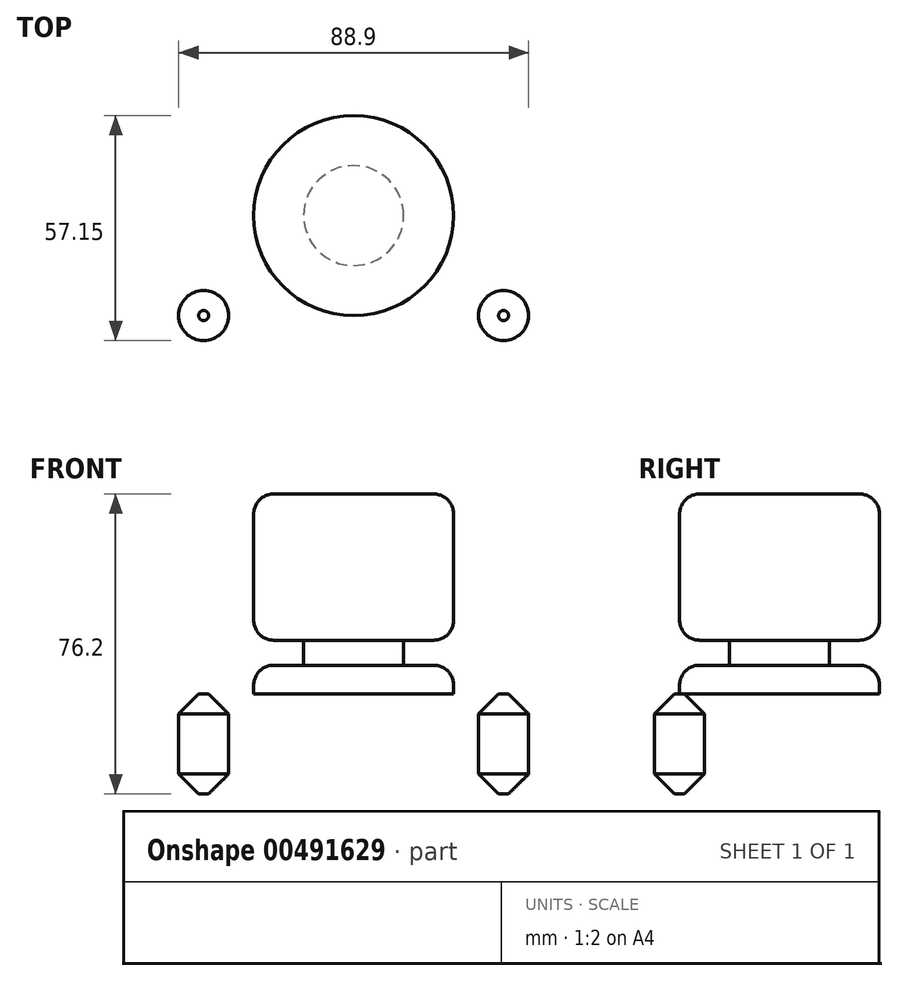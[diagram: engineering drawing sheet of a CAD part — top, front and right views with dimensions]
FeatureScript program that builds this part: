
annotation { "Feature Type Name" : "Feature", "Feature Type Description" : "" }
export const myFeature = defineFeature(function(context is Context, id is Id, definition is map)
    precondition{}
    {
        {
            var Q0;
            Q0=qCreatedBy(makeId("Top.planeOp"),FACE);
            var sketch = newSketch(context, id + "F0", { "sketchPlane" : qUnion([Q0])});
            skLineSegment(sketch, "E0.bottom", {"start": v(50.8, 38.1) * mm, "end": v(-50.8, 38.1) * mm});
            skLineSegment(sketch, "E0.top", {"start": v(50.8, -38.1) * mm, "end": v(-50.8, -38.1) * mm});
            skLineSegment(sketch, "E0.left", {"start": v(50.8, 38.1) * mm, "end": v(50.8, -38.1) * mm});
            skLineSegment(sketch, "E0.right", {"start": v(-50.8, 38.1) * mm, "end": v(-50.8, -38.1) * mm});
            skPoint(sketch, "E0.middle", {"position": v(0, 0) * mm});
            skSolve(sketch);
        }
        {
            var Q0;
            Q0 = qSketchRegion(id + "F0", true);
            extrude(context, id + "F1", {"entities" : qUnion([Q0]), "depth" : 25.4 * mm});
        }
        {
            var Q0;
            Q0=makeQuery(id+"F1.opExtrude","CAP_FACE",FACE,{"disambiguationData":[OSD([sQuery(id+"F0.wireOp",EDGE,"E0.bottom"),sQuery(id+"F0.wireOp",EDGE,"E0.top"),sQuery(id+"F0.wireOp",EDGE,"E0.left"),sQuery(id+"F0.wireOp",EDGE,"E0.right")])],"isStart":false});
            var sketch = newSketch(context, id + "F2", { "sketchPlane" : qUnion([Q0])});
            skCircle(sketch, "E1", {"center": v(-38.1, 25.4) * mm, "radius": 6.35 * mm});
            skCircle(sketch, "E2", {"center": v(38.1, 25.4) * mm, "radius": 6.35 * mm});
            skCircle(sketch, "E3.MirrorC", {"center": v(38.1, -25.4) * mm, "radius": 6.35 * mm});
            skCircle(sketch, "E4.MirrorC", {"center": v(-38.1, -25.4) * mm, "radius": 6.35 * mm});
            skSolve(sketch);
        }
        {
            var Q0;
            Q0=makeQuery(id+"F2.imprint","IMPRINT",FACE,{"disambiguationData":[TD([[makeQuery(id+"F2.imprint","IMPRINT",EDGE,{"derivedFrom":sQuery(id+"F2.wireOp",EDGE,"E1")}),1.0]])]});
            var Q1;
            Q1=makeQuery(id+"F2.imprint","IMPRINT",FACE,{"disambiguationData":[TD([[makeQuery(id+"F2.imprint","IMPRINT",EDGE,{"derivedFrom":sQuery(id+"F2.wireOp",EDGE,"E2")}),1.0]])]});
            var Q2;
            Q2=makeQuery(id+"F2.imprint","IMPRINT",FACE,{"disambiguationData":[TD([[makeQuery(id+"F2.imprint","IMPRINT",EDGE,{"derivedFrom":sQuery(id+"F2.wireOp",EDGE,"E3.MirrorC")}),-1.0]])]});
            var Q3;
            Q3=makeQuery(id+"F2.imprint","IMPRINT",FACE,{"disambiguationData":[TD([[makeQuery(id+"F2.imprint","IMPRINT",EDGE,{"derivedFrom":sQuery(id+"F2.wireOp",EDGE,"E4.MirrorC")}),-1.0]])]});
            var Q4;
            Q4=makeQuery(id+"F1.opExtrude","CAP_FACE",FACE,{"disambiguationData":[OSD([sQuery(id+"F0.wireOp",EDGE,"E0.bottom"),sQuery(id+"F0.wireOp",EDGE,"E0.top"),sQuery(id+"F0.wireOp",EDGE,"E0.left"),sQuery(id+"F0.wireOp",EDGE,"E0.right")])],"isStart":true});
            extrude(context, id + "F3", {"entities" : qUnion([Q0, Q1, Q2, Q3]), "operationType" : NewBodyOperationType.REMOVE, "endBound" : BoundingType.UP_TO_SURFACE, "oppositeDirection" : true, "endBoundEntityFace" : qUnion([Q4]), "depth" : 25.4 * mm});
        }
        {
            var Q0;
            Q0=makeQuery(id+"F1.opExtrude","CAP_FACE",FACE,{"disambiguationData":[OSD([sQuery(id+"F0.wireOp",EDGE,"E0.bottom"),sQuery(id+"F0.wireOp",EDGE,"E0.top"),sQuery(id+"F0.wireOp",EDGE,"E0.left"),sQuery(id+"F0.wireOp",EDGE,"E0.right")])],"isStart":false});
            var sketch = newSketch(context, id + "F4", { "sketchPlane" : qUnion([Q0])});
            skCircle(sketch, "E5", {"center": v(0, 0) * mm, "radius": 25.4 * mm});
            skSolve(sketch);
        }
        {
            var Q0;
            Q0=makeQuery(id+"F4.imprint","IMPRINT",FACE,{"disambiguationData":[TD([[makeQuery(id+"F4.imprint","IMPRINT",EDGE,{"derivedFrom":sQuery(id+"F4.wireOp",EDGE,"E5")}),1.0]])]});
            extrude(context, id + "F5", {"entities" : qUnion([Q0]), "operationType" : NewBodyOperationType.ADD, "depth" : 50.8 * mm});
        }
        {
            var Q0;
            Q0=qCreatedBy(makeId("Front.planeOp"),FACE);
            var sketch = newSketch(context, id + "F6", { "sketchPlane" : qUnion([Q0])});
            skLineSegment(sketch, "E6.bottom", {"start": v(-12.7, 32.7) * mm, "end": v(-73.97, 32.7) * mm});
            skLineSegment(sketch, "E6.top", {"start": v(-12.7, 39.06) * mm, "end": v(-73.97, 39.06) * mm});
            skLineSegment(sketch, "E6.left", {"start": v(-12.7, 32.7) * mm, "end": v(-12.7, 39.06) * mm});
            skLineSegment(sketch, "E6.right", {"start": v(-73.97, 32.7) * mm, "end": v(-73.97, 39.06) * mm});
            skPoint(sketch, "E6.middle", {"position": v(-43.34, 35.88) * mm});
            skLineSegment(sketch, "E7", {"start": v(0, 0) * mm, "end": v(0, 56.8) * mm});
            skSolve(sketch);
        }
        {
            var Q0;
            Q0=makeQuery(id+"F6.imprint","IMPRINT",FACE,{"disambiguationData":[TD([[makeQuery(id+"F6.imprint","IMPRINT",EDGE,{"derivedFrom":sQuery(id+"F6.wireOp",EDGE,"E6.bottom")}),-1.0]])]});
            var Q1;
            Q1=sQuery(id+"F6.wireOp",EDGE,"E7");
            revolve(context, id + "F7", {"operationType" : NewBodyOperationType.REMOVE, "entities" : qUnion([Q0]), "axis" : qUnion([Q1]), "revolveType" : RevolveType.FULL, "oppositeDirection" : true});
        }
        {
            var Q0;
            Q0=makeQuery(id+"F1.opExtrude","CAP_EDGE",EDGE,{"disambiguationData":[OSD([sQuery(id+"F0.wireOp",EDGE,"E0.top")])],"isStart":false});
            var Q1;
            Q1=makeQuery(id+"F7.boolean.opBoolean","INTERSECT",EDGE,{"derivedFrom":[makeQuery(id+"F5.opExtrude","SWEPT_FACE",FACE,{"disambiguationData":[OSD([sQuery(id+"F4.wireOp",EDGE,"E5")])]}),makeQuery(id+"F7.opRevolve","SWEPT_FACE",FACE,{"disambiguationData":[OSD([sQuery(id+"F6.wireOp",EDGE,"E6.bottom")])]})]});
            var Q2;
            Q2=makeQuery(id+"F7.boolean.opBoolean","INTERSECT",EDGE,{"derivedFrom":[makeQuery(id+"F5.opExtrude","SWEPT_FACE",FACE,{"disambiguationData":[OSD([sQuery(id+"F4.wireOp",EDGE,"E5")])]}),makeQuery(id+"F7.opRevolve","SWEPT_FACE",FACE,{"disambiguationData":[OSD([sQuery(id+"F6.wireOp",EDGE,"E6.top")])]})]});
            var Q3;
            Q3=makeQuery(id+"F5.opExtrude","CAP_EDGE",EDGE,{"disambiguationData":[OSD([sQuery(id+"F4.wireOp",EDGE,"E5")])],"isStart":false});
            var Q4;
            Q4=makeQuery(id+"F1.opExtrude","CAP_EDGE",EDGE,{"disambiguationData":[OSD([sQuery(id+"F0.wireOp",EDGE,"E0.left")])],"isStart":false});
            var Q5;
            Q5=makeQuery(id+"F1.opExtrude","CAP_EDGE",EDGE,{"disambiguationData":[OSD([sQuery(id+"F0.wireOp",EDGE,"E0.bottom")])],"isStart":false});
            var Q6;
            Q6=makeQuery(id+"F1.opExtrude","CAP_EDGE",EDGE,{"disambiguationData":[OSD([sQuery(id+"F0.wireOp",EDGE,"E0.right")])],"isStart":false});
            fillet(context, id + "F8", {"entities" : qUnion([Q0, Q1, Q2, Q3, Q4, Q5, Q6]), "radius" : 5.08 * mm, "tangentPropagation" : true, "allowEdgeOverflow" : false});
        }
        {
            var Q0;
            Q0=makeQuery(id+"F3.boolean.opBoolean","COPY",FACE,{"derivedFrom":makeQuery(id+"F3.opExtrude","SWEPT_FACE",FACE,{"disambiguationData":[OSD([sQuery(id+"F2.wireOp",EDGE,"E4.MirrorC")])]})});
            var Q1;
            Q1=makeQuery(id+"F3.boolean.opBoolean","COPY",FACE,{"derivedFrom":makeQuery(id+"F3.opExtrude","SWEPT_FACE",FACE,{"disambiguationData":[OSD([sQuery(id+"F2.wireOp",EDGE,"E1")])]})});
            var Q2;
            Q2=makeQuery(id+"F3.boolean.opBoolean","COPY",FACE,{"derivedFrom":makeQuery(id+"F3.opExtrude","SWEPT_FACE",FACE,{"disambiguationData":[OSD([sQuery(id+"F2.wireOp",EDGE,"E2")])]})});
            var Q3;
            Q3=makeQuery(id+"F3.boolean.opBoolean","COPY",FACE,{"derivedFrom":makeQuery(id+"F3.opExtrude","SWEPT_FACE",FACE,{"disambiguationData":[OSD([sQuery(id+"F2.wireOp",EDGE,"E3.MirrorC")])]})});
            chamfer(context, id + "F9", {"entities" : qUnion([Q0, Q1, Q2, Q3]), "width" : 5.08 * mm, "tangentPropagation" : true});
        }
    });
